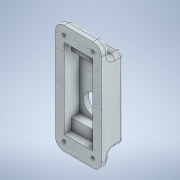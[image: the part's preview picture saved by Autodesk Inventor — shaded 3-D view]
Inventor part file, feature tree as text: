
AUTODESK INVENTOR PART (.ipt)
format: ipt  version: 2021 (Build 250183000, 183)  size: 274,432 bytes
history: native  units: mm
features: extrude x7, sketch x7, fillet x3
ambient origin geometry x8: Origin, YZ Plane, XZ Plane, XY Plane, X Axis, Y Axis, Z Axis, Center Point
bodies: Solid1 (feature_tree)
feature tree (17):
  extrude  "Extrusion1"  Depth=76.0mm
  fillet  "Fillet1"  Radius=16.0mm
  extrude  "Extrusion2"  Depth=20.0mm
  extrude  "Extrusion3"  Depth=18.0mm
  extrude  "Extrusion4"  Depth=10.5mm TaperAngle=0.0deg
  extrude  "Extrusion5"  Depth=10.0mm
  fillet  "Fillet2"  Radius=10.0mm
  extrude  "Extrusion6"  Depth=7.7mm
  extrude  "Extrusion7"  Depth=2.0mm
  fillet  "Fillet3"  Radius=5.0mm
  sketch  "Sketch1"  dims[d0=32.0mm d1=76.0mm d2=16.0mm d3=0.0mm]
  sketch  "Sketch2"  dims[d4=6.0mm d5=20.0mm]
  sketch  "Sketch3"  dims[d6=40.0mm d7=18.0mm]
  sketch  "Sketch4"  dims[d8=6.0mm d9=10.5mm d10=0.0mm]
  sketch  "Sketch5"  dims[d11=14.0mm d12=10.0mm d13=10.0mm]
  sketch  "Sketch6"  dims[d14=12.5mm d15=0.0mm d16=7.7mm]
  sketch  "Sketch7"  dims[d17=20.0mm d18=7.7mm d19=5.0mm d20=0.0mm d21=10.0mm d22=10.0mm d23=10.0mm d24=10.0mm d25=5.0mm d26=0.0mm d27=3.0mm d28=2.4mm d29=2.4mm d30=2.4mm d31=2.4mm d32=5.0mm d33=10.0mm d34=0.0mm d35=0.0mm d36=22.0mm d37=2.0mm d38=0.0mm d39=2.0mm]
